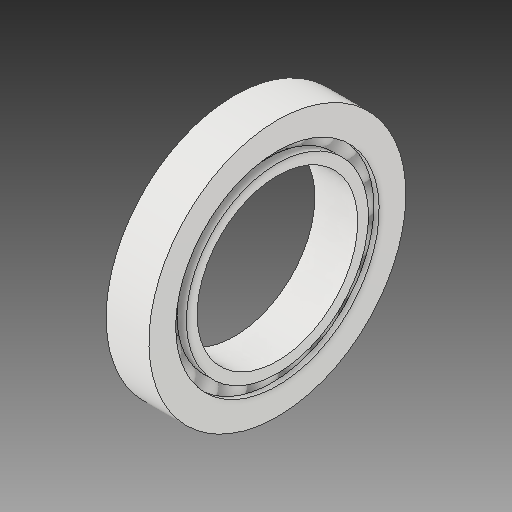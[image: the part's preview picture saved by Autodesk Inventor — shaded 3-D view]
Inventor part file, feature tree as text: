
AUTODESK INVENTOR PART (.ipt)
format: ipt  version: 2018 (Build 220112000, 112)  size: 411,136 bytes
history: native  units: mm
features: revolve x2, sketch x2, pattern_circular x1
ambient origin geometry x8: Origin, YZ Plane, XZ Plane, XY Plane, X Axis, Y Axis, Z Axis, Center Point
bodies: Solid1 (feature_tree)
feature tree (5):
  revolve  "Revolution1"  [1 undecoded]
  revolve  "Revolution2"  [1 undecoded]
  pattern_circular  "Circular Pattern1"  [2 undecoded]
  sketch  "Sketch1"  dims[d0=7.5mm d1=2.0mm]
  sketch  "Sketch2"  dims[d2=2.0mm d3=12.0mm d4=2.5mm d5=1.0mm d6=2.0mm d7=2.0mm d8=1.0mm d9=2.5mm d10=3.0mm d11=5.0mm d12=90.0deg d13=3.0mm d14=180.0deg d15=200.0mm d16=360.0deg]
note: 4 required parameter values undecoded (feature->parameter linkage not recoverable at this tier; creation-order binding heuristic only, values carry confidence <= 0.55)